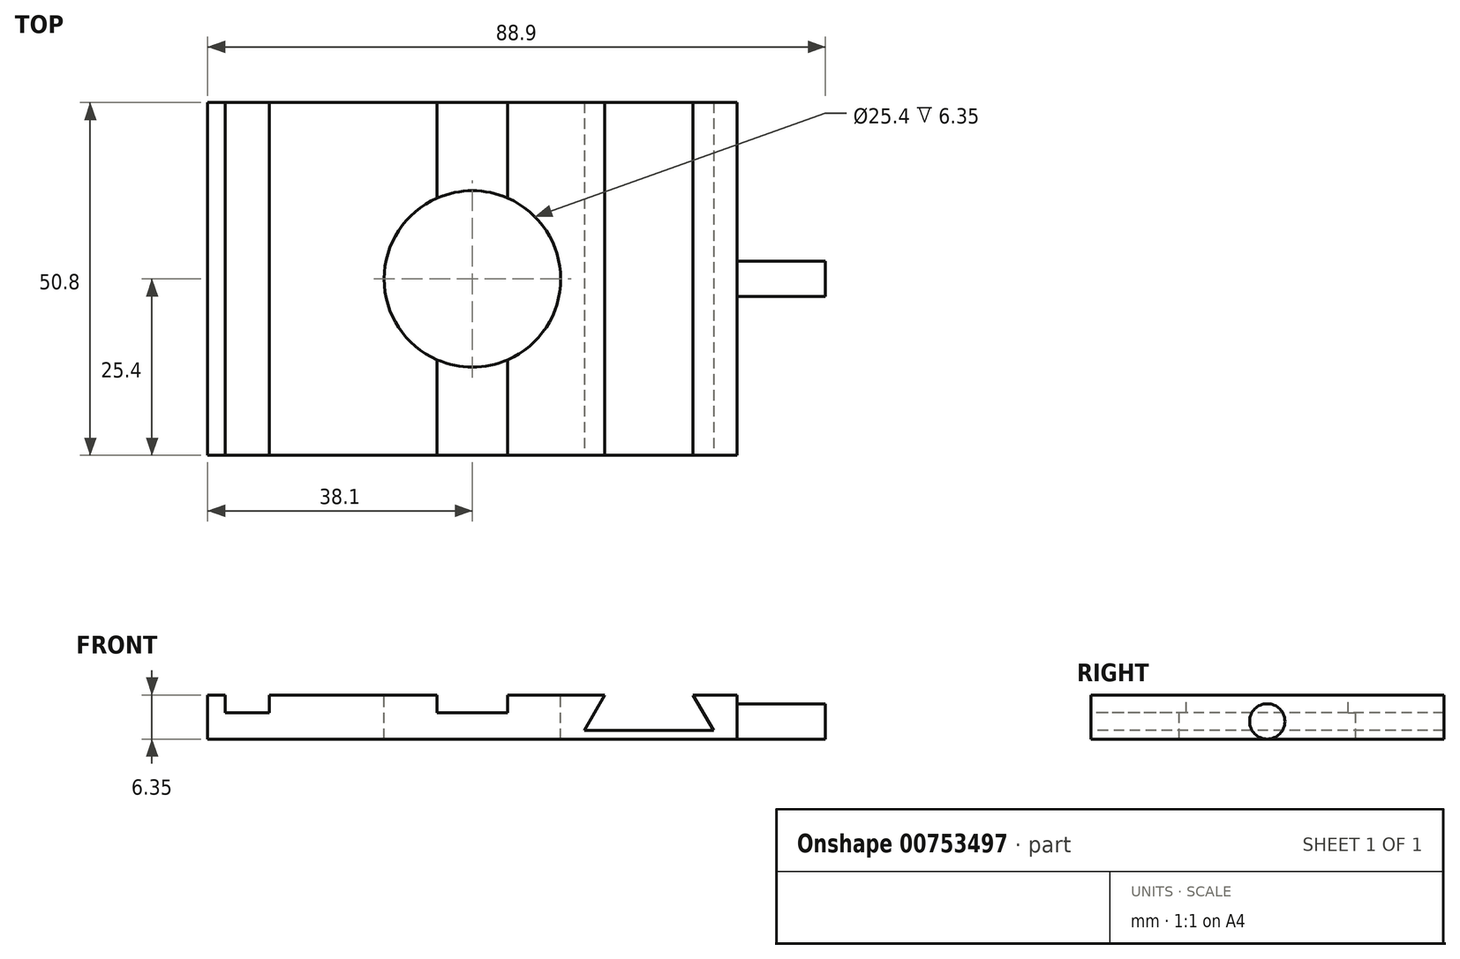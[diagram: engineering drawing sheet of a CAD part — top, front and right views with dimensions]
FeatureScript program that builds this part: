
annotation { "Feature Type Name" : "Feature", "Feature Type Description" : "" }
export const myFeature = defineFeature(function(context is Context, id is Id, definition is map)
    precondition{}
    {
        {
            var Q0;
            Q0=qCreatedBy(makeId("Top.planeOp"),FACE);
            var sketch = newSketch(context, id + "F0", { "sketchPlane" : qUnion([Q0])});
            skLineSegment(sketch, "E0.bottom", {"start": v(-38.1, 25.4) * mm, "end": v(38.1, 25.4) * mm});
            skLineSegment(sketch, "E0.top", {"start": v(-38.1, -25.4) * mm, "end": v(38.1, -25.4) * mm});
            skLineSegment(sketch, "E0.left", {"start": v(-38.1, 25.4) * mm, "end": v(-38.1, -25.4) * mm});
            skLineSegment(sketch, "E0.right", {"start": v(38.1, 25.4) * mm, "end": v(38.1, -25.4) * mm});
            skPoint(sketch, "E0.middle", {"position": v(0, 0) * mm});
            skCircle(sketch, "E1", {"center": v(0, 0) * mm, "radius": 12.7 * mm});
            skSolve(sketch);
        }
        {
            var Q0;
            Q0=makeQuery(id+"F0.imprint","IMPRINT",FACE,{"disambiguationData":[TD([[makeQuery(id+"F0.imprint","IMPRINT",EDGE,{"derivedFrom":sQuery(id+"F0.wireOp",EDGE,"E0.bottom")}),-1.0]])]});
            extrude(context, id + "F1", {"entities" : qUnion([Q0]), "oppositeDirection" : true, "depth" : 6.35 * mm, "offsetDistance" : 25.4 * mm});
        }
        {
            var Q0;
            Q0=makeQuery(id+"F1.opExtrude","CAP_FACE",FACE,{"disambiguationData":[OSD([sQuery(id+"F0.wireOp",EDGE,"E0.bottom"),sQuery(id+"F0.wireOp",EDGE,"E0.top"),sQuery(id+"F0.wireOp",EDGE,"E0.left"),sQuery(id+"F0.wireOp",EDGE,"E0.right"),sQuery(id+"F0.wireOp",EDGE,"E1")])],"isStart":true});
            var sketch = newSketch(context, id + "F2", { "sketchPlane" : qUnion([Q0])});
            skLineSegment(sketch, "E2.bottom", {"start": v(-35.56, 25.4) * mm, "end": v(-29.2, 25.4) * mm});
            skLineSegment(sketch, "E2.top", {"start": v(-35.56, -25.4) * mm, "end": v(-29.2, -25.4) * mm});
            skLineSegment(sketch, "E2.left", {"start": v(-35.56, 25.4) * mm, "end": v(-35.56, -25.4) * mm});
            skLineSegment(sketch, "E2.right", {"start": v(-29.2, 25.4) * mm, "end": v(-29.2, -25.4) * mm});
            skLineSegment(sketch, "E3", {"start": v(-5.08, 25.4) * mm, "end": v(-5.08, -25.4) * mm});
            skLineSegment(sketch, "E4", {"start": v(5.08, -25.4) * mm, "end": v(5.08, 25.4) * mm});
            skPoint(sketch, "E5", {"position": v(0, 0) * mm});
            skLineSegment(sketch, "E6", {"start": v(5.08, 25.4) * mm, "end": v(-5.08, 25.4) * mm, "construction": true});
            skLineSegment(sketch, "E7", {"start": v(0, 25.4) * mm, "end": v(0, -25.4) * mm, "construction": true});
            skSolve(sketch);
        }
        {
            var Q0;
            Q0=makeQuery(id+"F2.imprint","IMPRINT",FACE,{"disambiguationData":[TD([[makeQuery(id+"F2.imprint","IMPRINT",EDGE,{"derivedFrom":sQuery(id+"F2.wireOp",EDGE,"E2.bottom")}),-1.0]])]});
            var Q1;
            {var subQ0=sQuery(id+"F2.wireOp",EDGE,"E3");var subQ1=makeQuery(id+"F1.opExtrude","CAP_EDGE",EDGE,{"disambiguationData":[OSD([sQuery(id+"F0.wireOp",EDGE,"E0.top")])],"isStart":true});var subQ2=makeQuery(id+"F2.imprint","INTERSECT",VERTEX,{"derivedFrom":[subQ1,subQ0]});Q1=makeQuery(id+"F2.imprint","IMPRINT",FACE,{"disambiguationData":[TD([[makeQuery(id+"F2.imprint","IMPRINT",EDGE,{"disambiguationData":[TD([[subQ2,1.0]])],"derivedFrom":subQ0}),1.0]])]});}
            var Q2;
            {var subQ0=sQuery(id+"F2.wireOp",EDGE,"E3");var subQ1=makeQuery(id+"F1.opExtrude","CAP_EDGE",EDGE,{"disambiguationData":[OSD([sQuery(id+"F0.wireOp",EDGE,"E0.bottom")])],"isStart":true});var subQ2=makeQuery(id+"F2.imprint","INTERSECT",VERTEX,{"derivedFrom":[subQ1,subQ0]});Q2=makeQuery(id+"F2.imprint","IMPRINT",FACE,{"disambiguationData":[TD([[makeQuery(id+"F2.imprint","IMPRINT",EDGE,{"disambiguationData":[TD([[subQ2,-1.0]])],"derivedFrom":subQ0}),1.0]])]});}
            var Q3;
            Q3 = qSketchRegion(id + "F4", true);
            extrude(context, id + "F3", {"entities" : qUnion([Q0, Q1, Q2, Q3]), "operationType" : NewBodyOperationType.REMOVE, "oppositeDirection" : true, "depth" : 2.54 * mm, "offsetDistance" : 25.4 * mm});
        }
        {
            var Q0;
            Q0=qCreatedBy(makeId("Front.planeOp"),FACE);
            var sketch = newSketch(context, id + "F4", { "sketchPlane" : qUnion([Q0])});
            skLineSegment(sketch, "E8", {"start": v(19.05, 0) * mm, "end": v(16.12, -5.08) * mm});
            skLineSegment(sketch, "E9", {"start": v(16.12, -5.08) * mm, "end": v(34.69, -5.08) * mm});
            skLineSegment(sketch, "E10", {"start": v(34.69, -5.08) * mm, "end": v(31.75, 0) * mm});
            skLineSegment(sketch, "E11", {"start": v(31.75, 0) * mm, "end": v(19.05, 0) * mm});
            skLineSegment(sketch, "E12", {"start": v(25.4, 0) * mm, "end": v(25.4, -5.08) * mm, "construction": true});
            skSolve(sketch);
        }
        {
            var Q0;
            Q0 = qSketchRegion(id + "F4", true);
            extrude(context, id + "F5", {"entities" : qUnion([Q0]), "operationType" : NewBodyOperationType.REMOVE, "endBound" : BoundingType.SYMMETRIC, "oppositeDirection" : true, "depth" : 50.8 * mm, "offsetDistance" : 25.4 * mm});
        }
        {
            var Q0;
            Q0=makeQuery(id+"F1.opExtrude","SWEPT_FACE",FACE,{"disambiguationData":[OSD([sQuery(id+"F0.wireOp",EDGE,"E0.right")])]});
            var sketch = newSketch(context, id + "F6", { "sketchPlane" : qUnion([Q0])});
            skCircle(sketch, "E13", {"center": v(0, -3.81) * mm, "radius": 2.54 * mm});
            skSolve(sketch);
        }
        {
            var Q0;
            Q0 = qSketchRegion(id + "F6", true);
            extrude(context, id + "F7", {"entities" : qUnion([Q0]), "operationType" : NewBodyOperationType.ADD, "depth" : 12.7 * mm, "offsetDistance" : 25.4 * mm});
        }
    });
